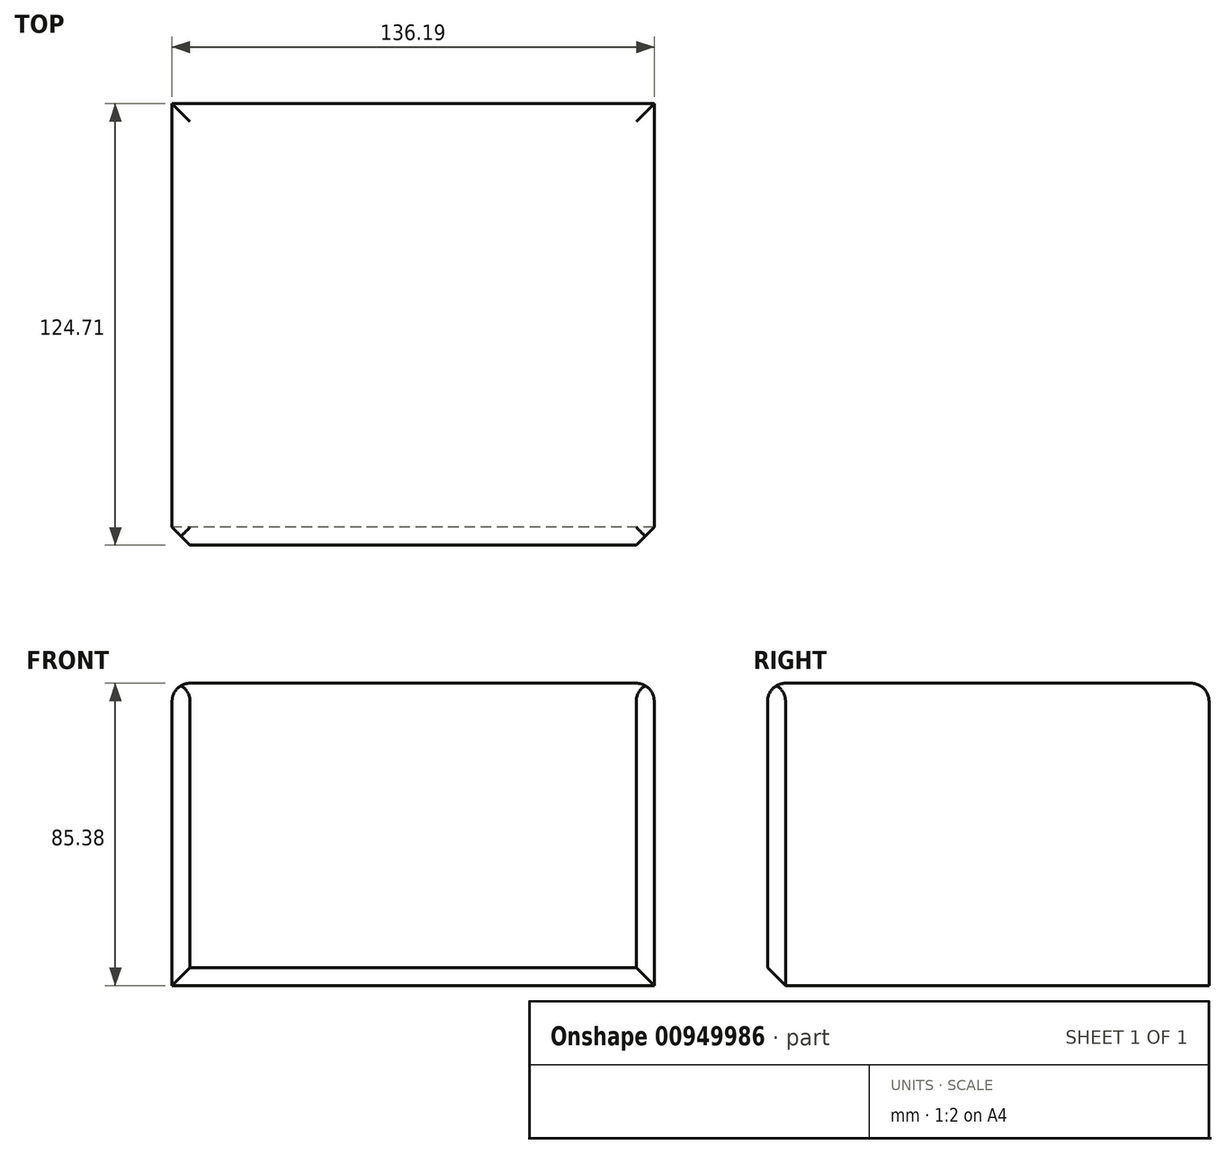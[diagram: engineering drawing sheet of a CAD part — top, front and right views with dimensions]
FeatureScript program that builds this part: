
annotation { "Feature Type Name" : "Feature", "Feature Type Description" : "" }
export const myFeature = defineFeature(function(context is Context, id is Id, definition is map)
    precondition{}
    {
        {
            var Q0;
            Q0=qCreatedBy(makeId("Front.planeOp"),FACE);
            var sketch = newSketch(context, id + "F0", { "sketchPlane" : qUnion([Q0])});
            skLineSegment(sketch, "E0.bottom", {"start": v(-68.45, 36.58) * mm, "end": v(67.74, 36.58) * mm});
            skLineSegment(sketch, "E0.top", {"start": v(-68.45, -48.8) * mm, "end": v(67.74, -48.8) * mm});
            skLineSegment(sketch, "E0.left", {"start": v(-68.45, 36.58) * mm, "end": v(-68.45, -48.8) * mm});
            skLineSegment(sketch, "E0.right", {"start": v(67.74, 36.58) * mm, "end": v(67.74, -48.8) * mm});
            skLineSegment(sketch, "E1.bottom", {"start": v(-27.04, 36.58) * mm, "end": v(0, 36.58) * mm});
            skLineSegment(sketch, "E1.top", {"start": v(-27.04, 86.1) * mm, "end": v(0, 86.1) * mm});
            skLineSegment(sketch, "E1.left", {"start": v(-27.04, 36.58) * mm, "end": v(-27.04, 86.1) * mm});
            skLineSegment(sketch, "E1.right", {"start": v(0, 36.58) * mm, "end": v(0, 86.1) * mm});
            skSolve(sketch);
        }
        {
            var Q0;
            Q0=makeQuery(id+"F0.imprint","IMPRINT",FACE,{"disambiguationData":[TD([[makeQuery(id+"F0.imprint","IMPRINT",EDGE,{"derivedFrom":sQuery(id+"F0.wireOp",EDGE,"E0.top")}),1.0]])]});
            extrude(context, id + "F1", {"entities" : qUnion([Q0]), "depth" : 124.7 * mm, "offsetDistance" : 25.4 * mm});
        }
        {
            var Q0;
            Q0=makeQuery(id+"F1.opExtrude","SWEPT_FACE",FACE,{"disambiguationData":[OSD([sQuery(id+"F0.wireOp",EDGE,"E0.bottom"),sQuery(id+"F0.wireOp",EDGE,"E1.bottom")])]});
            fillet(context, id + "F2", {"entities" : qUnion([Q0]), "radius" : 5.08 * mm, "tangentPropagation" : true, "allowEdgeOverflow" : false});
        }
        {
            var Q0;
            Q0=makeQuery(id+"F1.opExtrude","CAP_FACE",FACE,{"disambiguationData":[OSD([sQuery(id+"F0.wireOp",EDGE,"E0.bottom"),sQuery(id+"F0.wireOp",EDGE,"E0.top"),sQuery(id+"F0.wireOp",EDGE,"E0.left"),sQuery(id+"F0.wireOp",EDGE,"E0.right"),sQuery(id+"F0.wireOp",EDGE,"E1.bottom")])],"isStart":false});
            chamfer(context, id + "F3", {"entities" : qUnion([Q0]), "width" : 5.08 * mm, "tangentPropagation" : true});
        }
    });
